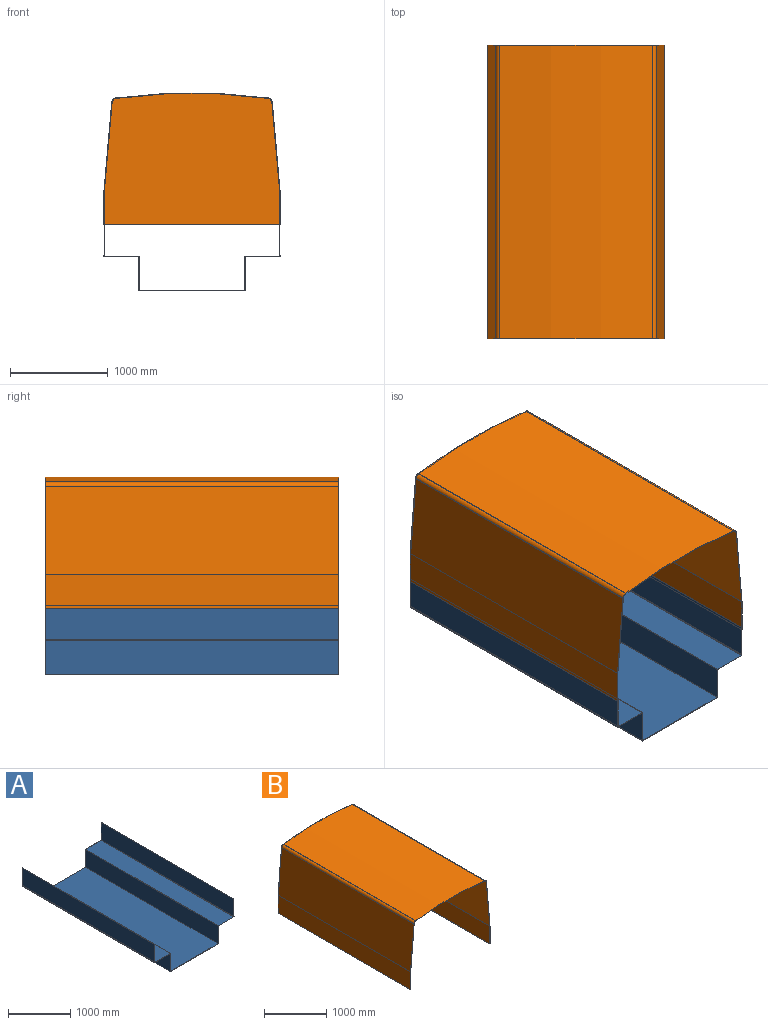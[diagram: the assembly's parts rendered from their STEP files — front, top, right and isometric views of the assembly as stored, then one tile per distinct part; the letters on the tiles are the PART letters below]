
ASSEMBLY  parts=2 mates=1
PART A: 22 faces, bbox 1800x3000x705 mm
  f0: plane 3000x350mm, normal (1,0,0), area 1050000mm2, adj f1,f19,f20,f21
  f1: plane 3000x350mm, normal (0,0,1), area 1050000mm2, adj f0,f2,f20,f21
  f2: plane 3000x350mm, normal (1,0,0), area 1050000mm2, adj f1,f3,f20,f21
  f3: plane 3000x5mm, normal (0,0,1), area 15000mm2, adj f2,f4,f20,f21
  f4: plane 3000x340mm, normal (-1,0,0), area 1020000.1mm2, adj f3,f5,f20,f21
  f5: plane 3000x5mm, normal (0,0,1), area 15000.1mm2, adj f4,f6,f20,f21
  f6: plane 3000x15mm, normal (-1,0,0), area 45000mm2, adj f5,f7,f20,f21
  f7: plane 3000x355mm, normal (0,0,-1), area 1065000mm2, adj f6,f8,f20,f21
  f8: plane 3000x350mm, normal (-1,0,0), area 1050000mm2, adj f7,f9,f20,f21
  f9: plane 3000x1090mm, normal (0,0,-1), area 3270000mm2, adj f8,f10,f20,f21
  f10: plane 3000x350mm, normal (1,0,0), area 1050000mm2, adj f9,f11,f20,f21
  f11: plane 3000x355mm, normal (0,0,-1), area 1065000mm2, adj f10,f12,f20,f21
  f12: plane 3000x15mm, normal (1,0,0), area 45000mm2, adj f11,f13,f20,f21
  f13: plane 3000x5mm, normal (0,0,1), area 15000.1mm2, adj f12,f14,f20,f21
  f14: plane 3000x340mm, normal (1,0,0), area 1020000.1mm2, adj f13,f15,f20,f21
  f15: plane 3000x5mm, normal (0,0,1), area 15000mm2, adj f14,f16,f20,f21
  f16: plane 3000x350mm, normal (-1,0,0), area 1050000mm2, adj f15,f17,f20,f21
  f17: plane 3000x350mm, normal (0,0,1), area 1050000mm2, adj f16,f18,f20,f21
  f18: plane 3000x350mm, normal (-1,0,0), area 1050000mm2, adj f17,f19,f20,f21
  f19: plane 3000x1080mm, normal (0,0,1), area 3239999.9mm2, adj f0,f18,f20,f21
  f20: plane 1800x705mm, normal (0,-1,0), area 16100.1mm2, adj f0,f1,f2,f3,f4,f5,f6,f7
  f21: plane 1800x705mm, normal (0,1,0), area 16100.1mm2, adj f0,f1,f2,f3,f4,f5,f6,f7
PART B: 18 faces, bbox 1800x3000x1350 mm
  f0: plane 3000x900.44mm, normal (-1,0,0.09), area 2711625.9mm2, adj f9,f10,f11,f16
  f1: plane 2995x900mm, normal (1,0,-0.09), area 2705796.4mm2, adj f2,f10,f12,f15
  f2: cylinder r=45mm len=2995mm, axis (0,1,0), area 181131.7mm2, adj f1,f3,f10,f12
  f3: cylinder r=5589.9mm len=2995mm, axis (0,1,0), area 4673418.9mm2, adj f2,f4,f10,f12
  f4: cylinder r=45mm len=2995mm, axis (0,1,0), area 181131.7mm2, adj f3,f5,f10,f12
  f5: plane 2995x900mm, normal (-1,0,-0.09), area 2705796.4mm2, adj f4,f10,f12,f14
  f6: plane 3000x900.44mm, normal (1,0,0.09), area 2711625.9mm2, adj f7,f10,f11,f13
  f7: cylinder r=50mm len=3000mm, axis (0,1,0), area 201593.4mm2, adj f6,f8,f10,f11
  f8: cylinder r=5594.9mm len=3000mm, axis (0,1,0), area 4685408.1mm2, adj f7,f9,f10,f11
  f9: cylinder r=50mm len=3000mm, axis (0,1,0), area 201593.4mm2, adj f0,f8,f10,f11
  f10: plane 1800x1350mm, normal (0,-1,0), area 20993.8mm2, adj f0,f1,f2,f3,f4,f5,f6,f7
  f11: plane 1800x1350mm, normal (0,1,0), area 2309526.3mm2, adj f0,f6,f7,f8,f9,f13,f16,f17
  f12: plane 1789.96x1345mm, normal (0,-1,0), area 2288532.5mm2, adj f1,f2,f3,f4,f5,f14,f15,f17
  f13: plane 3000x350mm, normal (1,0,0), area 1050000mm2, adj f6,f10,f11,f17
  f14: plane 2995x350mm, normal (-1,0,0), area 1048250mm2, adj f5,f10,f12,f17
  f15: plane 2995x350mm, normal (1,0,0), area 1048250mm2, adj f1,f10,f12,f17
  f16: plane 3000x350mm, normal (-1,0,0), area 1050000mm2, adj f0,f10,f11,f17
  f17: plane 3000x1800mm, normal (0,0,-1), area 39064.4mm2, adj f10,f11,f12,f13,f14,f15,f16
PLACE A t=(-3.5,-1476.78,-311.78)mm fixed
PLACE B t=(-3.48,23.22,8.22)mm
MATE slider A.f15 <-> B.f17  axis (0,0,1) through (891.5,-2976.78,-311.78)mm
